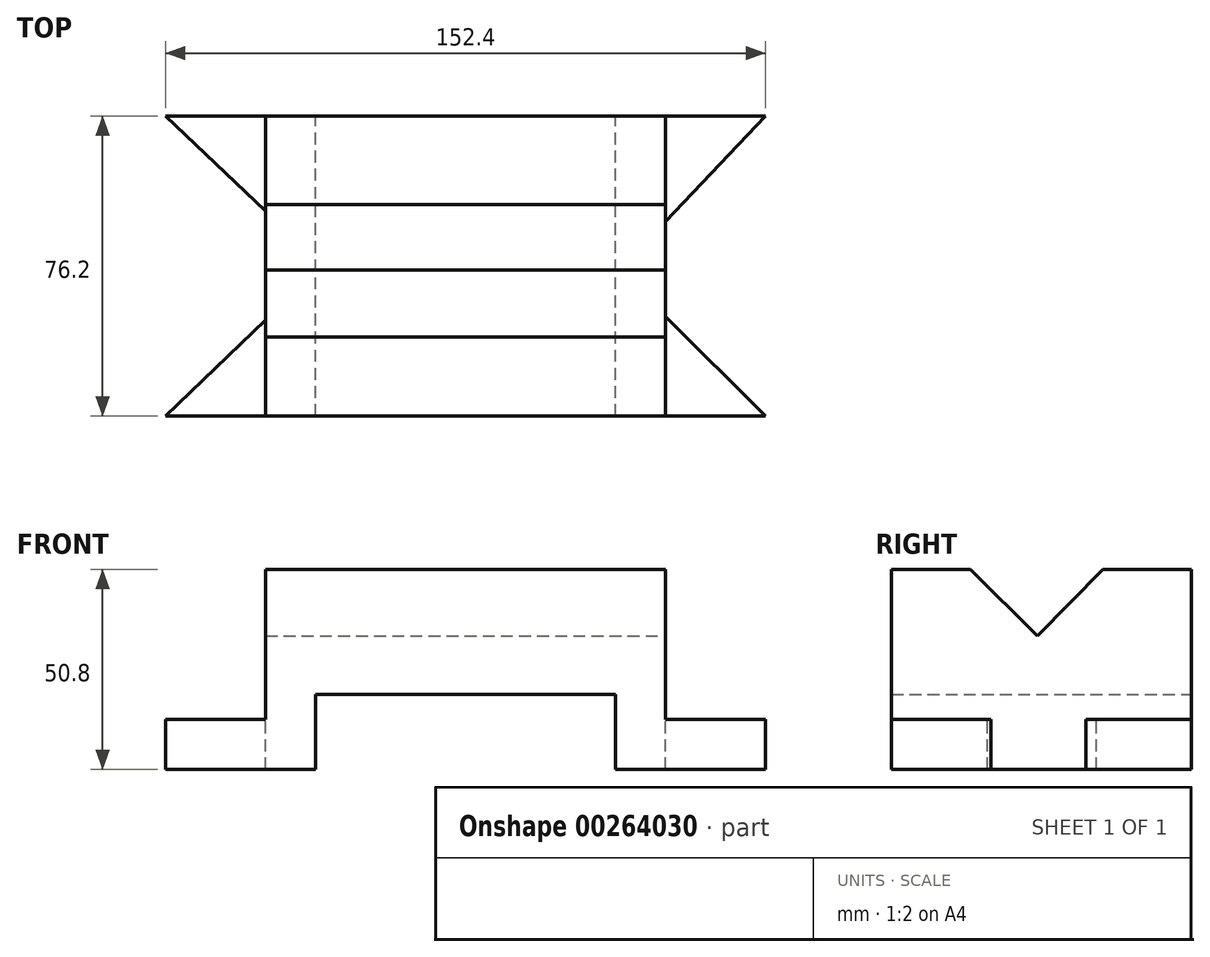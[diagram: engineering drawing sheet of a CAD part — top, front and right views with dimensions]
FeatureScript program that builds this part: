
annotation { "Feature Type Name" : "Feature", "Feature Type Description" : "" }
export const myFeature = defineFeature(function(context is Context, id is Id, definition is map)
    precondition{}
    {
        {
            var Q0;
            Q0=qCreatedBy(makeId("Front.planeOp"),FACE);
            var sketch = newSketch(context, id + "F0", { "sketchPlane" : qUnion([Q0])});
            skLineSegment(sketch, "E0", {"start": v(-75.98, 0) * mm, "end": v(-37.88, 0) * mm});
            skLineSegment(sketch, "E1", {"start": v(-75.98, 0) * mm, "end": v(-75.98, 12.7) * mm});
            skLineSegment(sketch, "E2", {"start": v(-75.98, 12.7) * mm, "end": v(-50.58, 12.7) * mm});
            skLineSegment(sketch, "E3", {"start": v(-50.58, 12.7) * mm, "end": v(-50.58, 50.8) * mm});
            skLineSegment(sketch, "E4", {"start": v(-50.58, 50.8) * mm, "end": v(51.02, 50.8) * mm});
            skLineSegment(sketch, "E5", {"start": v(51.02, 50.8) * mm, "end": v(51.02, 12.7) * mm});
            skLineSegment(sketch, "E6", {"start": v(51.02, 12.7) * mm, "end": v(76.42, 12.7) * mm});
            skLineSegment(sketch, "E7", {"start": v(76.42, 12.7) * mm, "end": v(76.42, 0) * mm});
            skLineSegment(sketch, "E8", {"start": v(76.42, 0) * mm, "end": v(38.32, 0) * mm});
            skLineSegment(sketch, "E9", {"start": v(38.32, 0) * mm, "end": v(38.32, 19.05) * mm});
            skLineSegment(sketch, "E10", {"start": v(38.32, 19.05) * mm, "end": v(-37.88, 19.05) * mm});
            skLineSegment(sketch, "E11", {"start": v(-37.88, 19.05) * mm, "end": v(-37.88, 0) * mm});
            skSolve(sketch);
        }
        {
            var Q0;
            Q0=makeQuery(id+"F0.imprint","IMPRINT",FACE,{"disambiguationData":[TD([[makeQuery(id+"F0.imprint","IMPRINT",EDGE,{"derivedFrom":sQuery(id+"F0.wireOp",EDGE,"E0")}),1.0]])]});
            extrude(context, id + "F1", {"entities" : qUnion([Q0]), "depth" : 76.2 * mm});
        }
        {
            var Q0;
            Q0=makeQuery(id+"F1.opExtrude","SWEPT_FACE",FACE,{"disambiguationData":[OSD([sQuery(id+"F0.wireOp",EDGE,"E6")])]});
            var sketch = newSketch(context, id + "F2", { "sketchPlane" : qUnion([Q0])});
            skLineSegment(sketch, "E12", {"start": v(76.42, -76.2) * mm, "end": v(51.02, -50.94) * mm});
            skLineSegment(sketch, "E13", {"start": v(76.42, 0) * mm, "end": v(51.02, -26.77) * mm});
            skLineSegment(sketch, "E14", {"start": v(76.42, -76.2) * mm, "end": v(76.42, 0) * mm});
            skLineSegment(sketch, "E15", {"start": v(51.02, -50.94) * mm, "end": v(51.02, -26.77) * mm});
            skSolve(sketch);
        }
        {
            var Q0;
            Q0=makeQuery(id+"F2.imprint","IMPRINT",FACE,{"disambiguationData":[TD([[makeQuery(id+"F2.imprint","IMPRINT",EDGE,{"derivedFrom":sQuery(id+"F2.wireOp",EDGE,"E12")}),-1.0]])]});
            extrude(context, id + "F3", {"entities" : qUnion([Q0]), "operationType" : NewBodyOperationType.REMOVE, "endBound" : BoundingType.UP_TO_NEXT, "oppositeDirection" : true, "depth" : 25.4 * mm});
        }
        {
            var Q0;
            Q0=makeQuery(id+"F1.opExtrude","SWEPT_FACE",FACE,{"disambiguationData":[OSD([sQuery(id+"F0.wireOp",EDGE,"E2")])]});
            var sketch = newSketch(context, id + "F4", { "sketchPlane" : qUnion([Q0])});
            skLineSegment(sketch, "E16", {"start": v(-75.98, -76.2) * mm, "end": v(-50.58, -51.8) * mm});
            skLineSegment(sketch, "E17", {"start": v(-75.98, 0) * mm, "end": v(-50.58, -24.18) * mm});
            skLineSegment(sketch, "E18", {"start": v(-50.58, -24.18) * mm, "end": v(-50.58, -51.8) * mm});
            skLineSegment(sketch, "E19", {"start": v(-75.98, 0) * mm, "end": v(-75.98, -76.2) * mm});
            skSolve(sketch);
        }
        {
            var Q0;
            Q0=makeQuery(id+"F4.imprint","IMPRINT",FACE,{"disambiguationData":[TD([[makeQuery(id+"F4.imprint","IMPRINT",EDGE,{"derivedFrom":sQuery(id+"F4.wireOp",EDGE,"E16")}),1.0]])]});
            extrude(context, id + "F5", {"entities" : qUnion([Q0]), "operationType" : NewBodyOperationType.REMOVE, "endBound" : BoundingType.UP_TO_NEXT, "oppositeDirection" : true, "depth" : 25.4 * mm});
        }
        {
            var Q0;
            Q0=makeQuery(id+"F3.boolean.opBoolean","MERGE",FACE,{"derivedFrom":[makeQuery(id+"F1.opExtrude","SWEPT_FACE",FACE,{"disambiguationData":[OSD([sQuery(id+"F0.wireOp",EDGE,"E5")])]}),makeQuery(id+"F3.opExtrude","SWEPT_FACE",FACE,{"disambiguationData":[OSD([sQuery(id+"F2.wireOp",EDGE,"E15")])]})]});
            var sketch = newSketch(context, id + "F6", { "sketchPlane" : qUnion([Q0])});
            skLineSegment(sketch, "E20", {"start": v(-39.14, 33.96) * mm, "end": v(-22.45, 50.8) * mm});
            skLineSegment(sketch, "E21", {"start": v(-39.14, 33.96) * mm, "end": v(-56.13, 50.8) * mm});
            skLineSegment(sketch, "E22", {"start": v(-56.13, 50.8) * mm, "end": v(-22.45, 50.8) * mm});
            skSolve(sketch);
        }
        {
            var Q0;
            Q0=makeQuery(id+"F6.imprint","IMPRINT",FACE,{"disambiguationData":[TD([[makeQuery(id+"F6.imprint","IMPRINT",EDGE,{"derivedFrom":sQuery(id+"F6.wireOp",EDGE,"E20")}),1.0]])]});
            extrude(context, id + "F7", {"entities" : qUnion([Q0]), "operationType" : NewBodyOperationType.REMOVE, "endBound" : BoundingType.UP_TO_NEXT, "oppositeDirection" : true, "depth" : 25.4 * mm});
        }
    });
